# Revit family: 4461_Addressable Multipurpose IO Unit
name_source: partatom
category: Fire Alarm Devices
units: mm (PartAtom-declared; Revit-internal decimal feet)

## family parameters
Cut with Voids When Loaded = No
Host = Face
Maintain Annotation Orientation = No
OmniClass Number = 23.85.30.21
OmniClass Title = Environmental Detection/Registration
Part Type = Normal
Room Calculation Point = No
Round Connector Dimension = Use Diameter
Shared = No

## types (1)
- 4461
    Ambient Humidity = Maximum 95 % RH
    Ambient Temperature Operating = -10 to +50 °C
    Ambient Temperature Storage = -20 to +60 °C
    CPR = 0786-CPR-21579
    Current (Active) = ≤ 15 mA
    Current Quiescent = ≤ 4.3 mA
    Default Elevation = 0 mm  [stored 0 ft]
    Depth (mm) = 49 mm  [stored 0.160761 ft]
    Description = Addressable multipurpose I/O unit with isolator 4461
    Enclosure = Standard Fibox encapsulation. (JB 6 G)
    General Inputs = 1
    Height (mm) = 110 mm  [stored 0.360892 ft]
    Ingress Protection Rating = IP65
    Isolated Inputs (Optocoupler Inputs) = 1
    Manufacturer = Panasonic
    Max_Wire Size = Ø 1.2 mm (1.5 mm²)
    Min_Wire Size = Ø 0.6 mm (0.28 mm²)
    Model = 4461
    Monitored Inputs = 1
    Omniclass Code = 23.85.30.21.11.11.11
    Omniclass Description = Smoke Detectors
    Power Supply = Via COM loop
    Product Material = Polycarbonate_Panasonic_White
    Relay Outputs = 2
    Short Circuit Isolator = Yes (Built-in)
    Tested and Approved = EN54-18, EN54-17
    Type Comments = The 4461 is a multipurpose I/O for connection of various units and equipment to the loop. The unit has two programmable relay outputs, one monitored input, one isolated input and one general input. All inputs and outputs are programmed via EBLWin
    URL = https://www.panasonic-fire-security.com
    Uniclass 2015 Code = Pr_75_80_30_27
    Uniclass 2015 Description = Fire and smoke detector bases
    Uniformat 2010  Code = D7050
    Uniformat 2010 Description = Detection and Alarm
    Vds Approval = G218074
    Version = RVT20
    Voltage Allowed = 12 – 30 VDC
    Voltage Normal = 24 VDC
    Weight = 188g
    Width (mm) = 110 mm  [stored 0.360892 ft]

note: [stored X ft] marks values corroborated as IEEE doubles in the binary element streams (Revit-internal decimal feet)

## geometry (parser evidence)
native form markers: Blend x83, Sweep x2
no freeform markers — native parametric forms only
